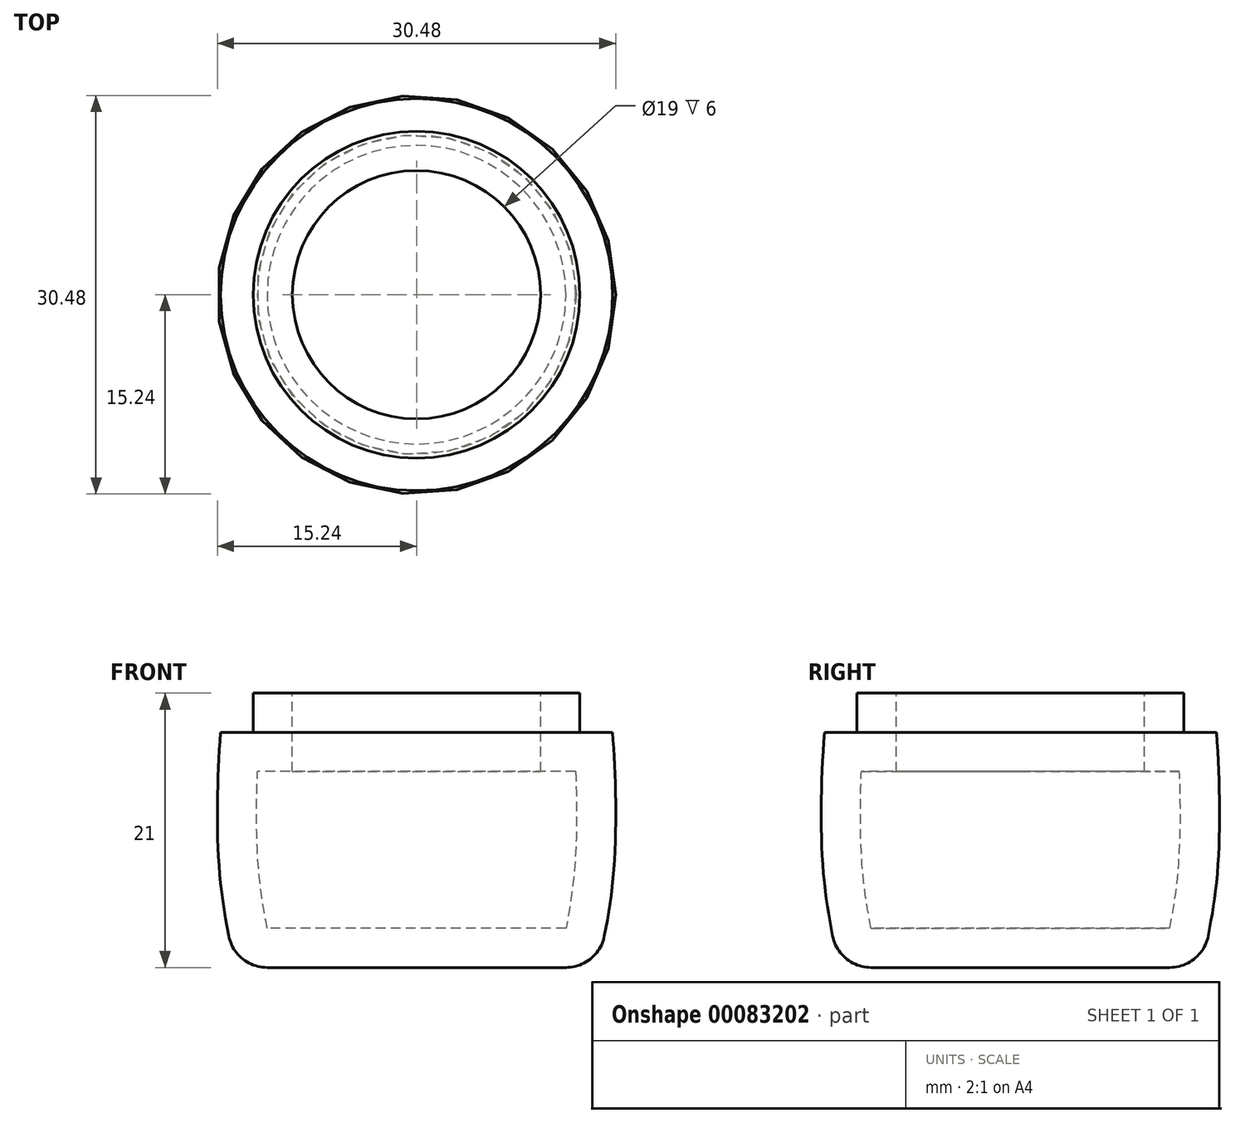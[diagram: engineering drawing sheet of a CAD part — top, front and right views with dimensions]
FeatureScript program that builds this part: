
annotation { "Feature Type Name" : "Feature", "Feature Type Description" : "" }
export const myFeature = defineFeature(function(context is Context, id is Id, definition is map)
    precondition{}
    {
        {
            var Q0;
            Q0=qCreatedBy(makeId("Front.planeOp"),FACE);
            var sketch = newSketch(context, id + "F0", { "sketchPlane" : qUnion([Q0])});
            skLineSegment(sketch, "E0.bottom", {"start": v(17.5, -25) * mm, "end": v(-17.5, -25) * mm});
            skLineSegment(sketch, "E0.top", {"start": v(17.5, 25) * mm, "end": v(-17.5, 25) * mm});
            skLineSegment(sketch, "E0.left", {"start": v(17.5, -25) * mm, "end": v(17.5, 25) * mm});
            skLineSegment(sketch, "E0.right", {"start": v(-17.5, -25) * mm, "end": v(-17.5, 25) * mm});
            skPoint(sketch, "E0.middle", {"position": v(0, 0) * mm});
            skLineSegment(sketch, "E1", {"start": v(-27.91, -5) * mm, "end": v(35.26, -5) * mm});
            skSolve(sketch);
        }
        {
            var Q0;
            {var subQ0=sQuery(id+"F0.wireOp",EDGE,"E0.bottom");Q0=makeQuery(id+"F0.imprint","IMPRINT",FACE,{"disambiguationData":[TD([[makeQuery(id+"F0.imprint","IMPRINT",EDGE,{"derivedFrom":subQ0}),-1.0]])]});}
            var sketch = newSketch(context, id + "F1", { "sketchPlane" : qUnion([Q0])});
            skFitSpline(sketch, "E2", {"points": [v(-14.94, -4.31) * mm, v(-15.08, -15.65) * mm, v(-13.44, -25.17) * mm], "startDerivative": vector(-1.46, -16.7) * mm, "endDerivative": vector(3.95, -20.47) * mm});
            skPoint(sketch, "E3.0", {"position": v(-27.91, -5) * mm});
            skLineSegment(sketch, "E4", {"start": v(-15, -5) * mm, "end": v(-12.5, -5) * mm});
            skLineSegment(sketch, "E5", {"start": v(0, -2) * mm, "end": v(0, -25) * mm});
            skPoint(sketch, "E6.0", {"position": v(-17.5, -25) * mm});
            skLineSegment(sketch, "E7", {"start": v(-12.5, -2) * mm, "end": v(1.91, -2) * mm});
            skLineSegment(sketch, "E8", {"start": v(-12.5, -5) * mm, "end": v(-12.5, -2) * mm});
            skPoint(sketch, "E9.orphan", {"position": v(0, -5) * mm});
            skLineSegment(sketch, "E10", {"start": v(-13.88, -23) * mm, "end": v(0, -23) * mm});
            skSolve(sketch);
        }
        {
            var Q0;
            Q0=qSketchRegion(id+"F1",true);
            var Q1;
            Q1=sQuery(id+"F1.wireOp",EDGE,"E5");
            revolve(context, id + "F2", {"entities" : qUnion([Q0]), "axis" : qUnion([Q1]), "revolveType" : RevolveType.FULL});
        }
        {
            var Q0;
            Q0=makeQuery(id+"F2.opRevolve","SWEPT_FACE",FACE,{"disambiguationData":[OSD([sQuery(id+"F1.wireOp",EDGE,"E7")])]});
            shell(context, id + "F3", {"entities" : qUnion([Q0]), "thickness" : 3 * mm});
        }
        {
            var Q0;
            Q0=makeQuery(id+"F2.opRevolve","SWEPT_EDGE",EDGE,{"disambiguationData":[OSD([sQuery(id+"F1.wireOp",EDGE,"E2"),sQuery(id+"F1.wireOp",EDGE,"E10")])]});
            fillet(context, id + "F4", {"entities" : qUnion([Q0]), "radius" : 3 * mm, "tangentPropagation" : true, "allowEdgeOverflow" : false});
        }
    });
